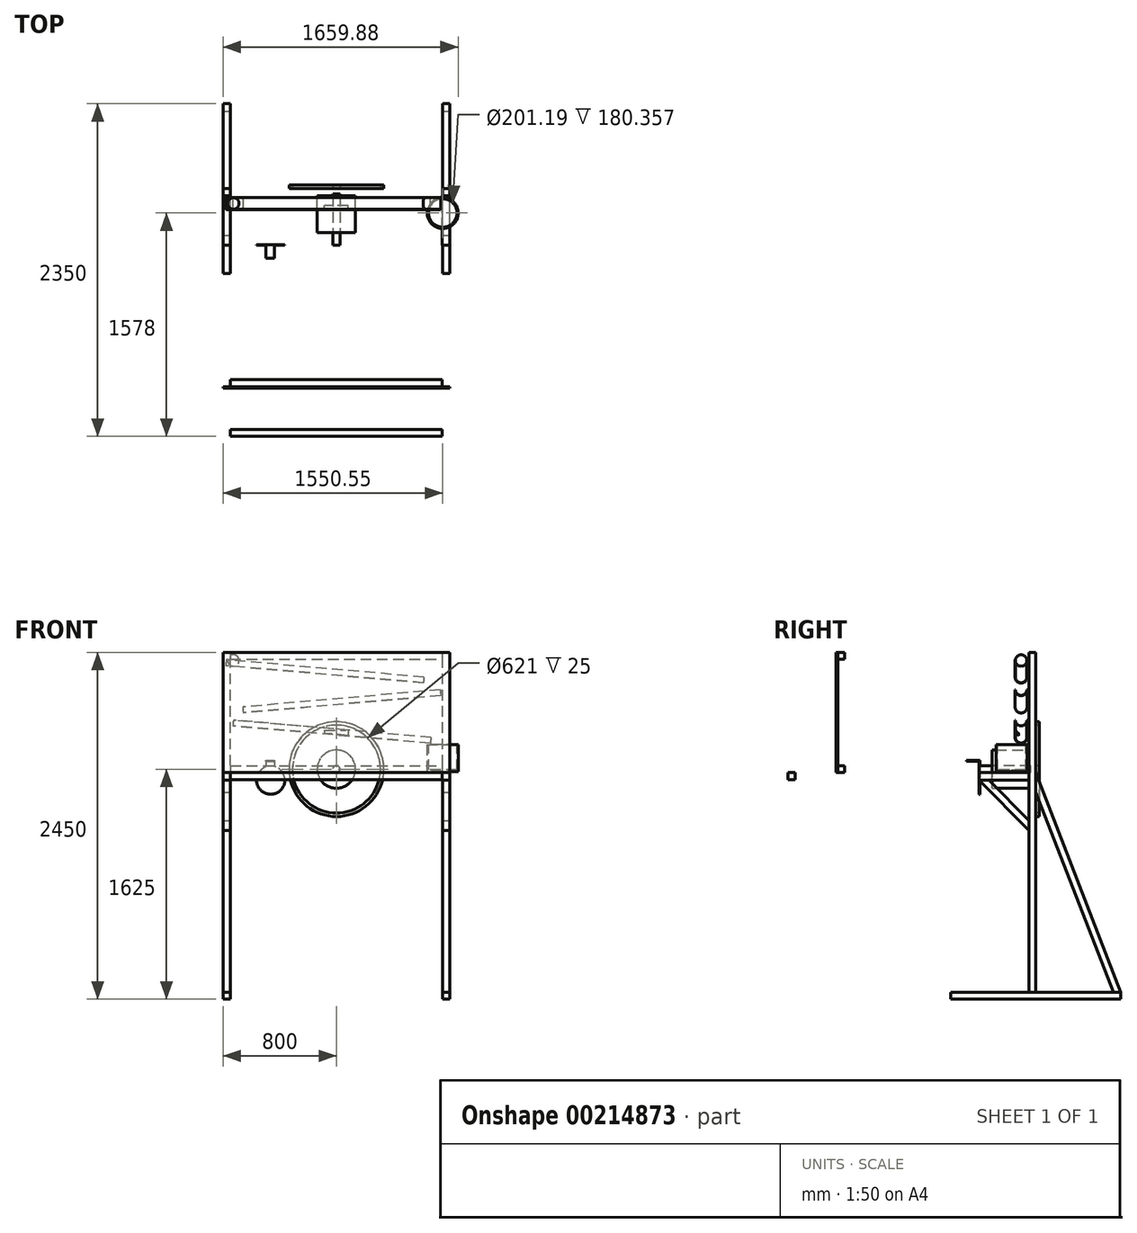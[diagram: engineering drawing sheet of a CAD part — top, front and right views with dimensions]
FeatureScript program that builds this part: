
annotation { "Feature Type Name" : "Feature", "Feature Type Description" : "" }
export const myFeature = defineFeature(function(context is Context, id is Id, definition is map)
    precondition{}
    {
        {
            var Q0;
            Q0=qCreatedBy(makeId("Front.planeOp"),FACE);
            var sketch = newSketch(context, id + "F0", { "sketchPlane" : qUnion([Q0])});
            skLineSegment(sketch, "E0.bottom", {"start": v(-225, 0) * mm, "end": v(225, 0) * mm});
            skLineSegment(sketch, "E0.top", {"start": v(-225, 450) * mm, "end": v(225, 450) * mm});
            skLineSegment(sketch, "E0.left", {"start": v(-225, 0) * mm, "end": v(-225, 450) * mm});
            skLineSegment(sketch, "E0.right", {"start": v(225, 0) * mm, "end": v(225, 450) * mm});
            skLineSegment(sketch, "E1", {"start": v(0, 450) * mm, "end": v(0, 1150) * mm});
            skEllipse(sketch, "E2", {"center": v(0, 800) * mm, "majorRadius": 350 * mm, "minorRadius": 176.3 * mm, "majorAxis": v(0, 1)});
            skLineSegment(sketch, "E3", {"start": v(0, 1150) * mm, "end": v(0, 1400) * mm});
            skCircle(sketch, "E4", {"center": v(0, 1275) * mm, "radius": 125 * mm});
            skSolve(sketch);
        }
        {
            var Q0;
            Q0=qCreatedBy(makeId("Front.planeOp"),FACE);
            var sketch = newSketch(context, id + "F1", { "sketchPlane" : qUnion([Q0])});
            skLineSegment(sketch, "E5.top", {"start": v(800, 2400) * mm, "end": v(750, 2400) * mm});
            skLineSegment(sketch, "E5.left", {"start": v(800, 0) * mm, "end": v(800, 2400) * mm});
            skLineSegment(sketch, "E5.right", {"start": v(750, 0) * mm, "end": v(750, 2400) * mm});
            skLineSegment(sketch, "E6.top", {"start": v(-800, 2400) * mm, "end": v(-750, 2400) * mm});
            skLineSegment(sketch, "E6.left", {"start": v(-800, 0) * mm, "end": v(-800, 2400) * mm});
            skLineSegment(sketch, "E6.right", {"start": v(-750, 0) * mm, "end": v(-750, 2400) * mm});
            skLineSegment(sketch, "E7.bottom", {"start": v(-749.4, 2400) * mm, "end": v(746.98, 2400) * mm});
            skLineSegment(sketch, "E7.top", {"start": v(-749.4, 2350) * mm, "end": v(746.98, 2350) * mm});
            skLineSegment(sketch, "E7.left", {"start": v(-749.4, 2400) * mm, "end": v(-749.4, 2350) * mm});
            skLineSegment(sketch, "E7.right", {"start": v(746.98, 2400) * mm, "end": v(746.98, 2350) * mm});
            skLineSegment(sketch, "E8.bottom", {"start": v(-748.32, 1600) * mm, "end": v(748.04, 1600) * mm});
            skLineSegment(sketch, "E8.top", {"start": v(-748.32, 1550) * mm, "end": v(748.04, 1550) * mm});
            skLineSegment(sketch, "E8.left", {"start": v(-748.32, 1600) * mm, "end": v(-748.32, 1550) * mm});
            skLineSegment(sketch, "E8.right", {"start": v(748.04, 1600) * mm, "end": v(748.04, 1550) * mm});
            skLineSegment(sketch, "E9", {"start": v(-800, 0) * mm, "end": v(-750, 0) * mm});
            skPoint(sketch, "E6.bottom.start.orphan", {"position": v(-800, 0) * mm});
            skLineSegment(sketch, "E10.trimOffspring", {"start": v(750, 0) * mm, "end": v(800, 0) * mm});
            skPoint(sketch, "E11.orphan", {"position": v(800, 0) * mm});
            skSolve(sketch);
        }
        {
            var Q0;
            Q0 = qSketchRegion(id + "F1", true);
            extrude(context, id + "F2", {"entities" : qUnion([Q0]), "depth" : 50 * mm, "offsetDistance" : 25 * mm});
        }
        {
            var Q0;
            Q0=makeQuery(id+"F2.opExtrude","CAP_FACE",FACE,{"disambiguationData":[OSD([sQuery(id+"F1.wireOp",EDGE,"E6.bottom"),sQuery(id+"F1.wireOp",EDGE,"E6.top"),sQuery(id+"F1.wireOp",EDGE,"E6.left"),sQuery(id+"F1.wireOp",EDGE,"E6.right")])],"isStart":false});
            var sketch = newSketch(context, id + "F3", { "sketchPlane" : qUnion([Q0])});
            skLineSegment(sketch, "E12.0", {"start": v(-748.32, 1550) * mm, "end": v(748.04, 1550) * mm, "construction": true});
            skLineSegment(sketch, "E13.0", {"start": v(800, 0) * mm, "end": v(800, 2400) * mm, "construction": true});
            skLineSegment(sketch, "E14.0", {"start": v(-800, 0) * mm, "end": v(-800, 2400) * mm, "construction": true});
            skLineSegment(sketch, "E15.bottom", {"start": v(-800, 2400) * mm, "end": v(800, 2400) * mm});
            skLineSegment(sketch, "E15.top", {"start": v(-800, 1550) * mm, "end": v(800, 1550) * mm});
            skLineSegment(sketch, "E15.left", {"start": v(-800, 2400) * mm, "end": v(-800, 1550) * mm});
            skLineSegment(sketch, "E15.right", {"start": v(800, 2400) * mm, "end": v(800, 1550) * mm});
            skSolve(sketch);
        }
        {
            var Q0;
            Q0 = qSketchRegion(id + "F3", true);
            extrude(context, id + "F4", {"entities" : qUnion([Q0]), "depth" : 10 * mm, "offsetDistance" : 25 * mm});
        }
        {
            var Q0;
            Q0=qCreatedBy(makeId("Right.planeOp"),FACE);
            var sketch = newSketch(context, id + "F5", { "sketchPlane" : qUnion([Q0])});
            skArc(sketch, "E16", {"start": v(-146.99, 2435.9) * mm, "mid": v(-104.43, 2393.34) * mm, "end": v(-61.88, 2435.9) * mm});
            skArc(sketch, "E17", {"start": v(-144.88, 2435.9) * mm, "mid": v(-104.43, 2395.46) * mm, "end": v(-64, 2435.9) * mm});
            skLineSegment(sketch, "E18", {"start": v(-64, 2435.9) * mm, "end": v(-61.88, 2435.9) * mm});
            skLineSegment(sketch, "E19", {"start": v(-144.88, 2435.9) * mm, "end": v(-146.99, 2435.9) * mm});
            skSolve(sketch);
        }
        {
            var Q0;
            Q0 = qSketchRegion(id + "F5", true);
            extrude(context, id + "F6", {"entities" : qUnion([Q0]), "endBound" : BoundingType.SYMMETRIC, "depth" : 1400 * mm, "offsetDistance" : 25 * mm});
        }
        {
            var Q0;
            Q0=makeQuery(id+"F6.opExtrude","SWEPT_BODY",BODY,{"disambiguationData":[OSD([sQuery(id+"F5.wireOp",EDGE,"E16"),sQuery(id+"F5.wireOp",EDGE,"E17"),sQuery(id+"F5.wireOp",EDGE,"E18"),sQuery(id+"F5.wireOp",EDGE,"E19")])]});
            var Q1;
            Q1=sQuery(id+"F5.wireOp",EDGE,"E19");
            transform(context, id + "F7", {"entities" : qUnion([Q0]), "transformType" : TransformType.ROTATION, "transformAxis" : qUnion([Q1]), "angle" : 5 * degree, "oppositeDirection" : true, "makeCopy" : false});
        }
        {
            var Q0;
            Q0=makeQuery(id+"F6.opExtrude","SWEPT_BODY",BODY,{"disambiguationData":[OSD([sQuery(id+"F5.wireOp",EDGE,"E16"),sQuery(id+"F5.wireOp",EDGE,"E17"),sQuery(id+"F5.wireOp",EDGE,"E18"),sQuery(id+"F5.wireOp",EDGE,"E19")])]});
            transform(context, id + "F8", {"entities" : qUnion([Q0]), "transformType" : TransformType.TRANSLATION_3D, "dx" : -80 * mm, "dy" : 0 * mm, "dz" : -150 * mm, "makeCopy" : false});
        }
        {
            var Q0;
            Q0=makeQuery(id+"F6.opExtrude","SWEPT_BODY",BODY,{"disambiguationData":[OSD([sQuery(id+"F5.wireOp",EDGE,"E16"),sQuery(id+"F5.wireOp",EDGE,"E17"),sQuery(id+"F5.wireOp",EDGE,"E18"),sQuery(id+"F5.wireOp",EDGE,"E19")])]});
            transform(context, id + "F9", {"entities" : qUnion([Q0]), "transformType" : TransformType.TRANSLATION_3D, "dx" : 116 * mm, "dy" : 0 * mm, "dz" : -89 * mm, "makeCopy" : true});
        }
        {
            var Q0;
            Q0=makeQuery(id+"F9.opPattern","COPY",BODY,{"derivedFrom":makeQuery(id+"F6.opExtrude","SWEPT_BODY",BODY,{"disambiguationData":[OSD([sQuery(id+"F5.wireOp",EDGE,"E16"),sQuery(id+"F5.wireOp",EDGE,"E17"),sQuery(id+"F5.wireOp",EDGE,"E18"),sQuery(id+"F5.wireOp",EDGE,"E19")])]}),"instanceName":"1"});
            var Q1;
            Q1=makeQuery(id+"F9.opPattern","COPY",EDGE,{"derivedFrom":makeQuery(id+"F6.opExtrude","CAP_EDGE",EDGE,{"disambiguationData":[OSD([sQuery(id+"F5.wireOp",EDGE,"E19")])],"isStart":false}),"instanceName":"1"});
            transform(context, id + "F10", {"entities" : qUnion([Q0]), "transformType" : TransformType.ROTATION, "transformAxis" : qUnion([Q1]), "angle" : 10 * degree, "makeCopy" : false});
        }
        {
            var Q0;
            Q0=makeQuery(id+"F6.opExtrude","SWEPT_BODY",BODY,{"disambiguationData":[OSD([sQuery(id+"F5.wireOp",EDGE,"E16"),sQuery(id+"F5.wireOp",EDGE,"E17"),sQuery(id+"F5.wireOp",EDGE,"E18"),sQuery(id+"F5.wireOp",EDGE,"E19")])]});
            transform(context, id + "F11", {"entities" : qUnion([Q0]), "transformType" : TransformType.TRANSLATION_3D, "dx" : 50 * mm, "dy" : 0 * mm, "dz" : -426 * mm, "makeCopy" : true});
        }
        {
            var Q0;
            Q0=makeQuery(id+"F2.opExtrude","CAP_FACE",FACE,{"disambiguationData":[OSD([sQuery(id+"F1.wireOp",EDGE,"E5.bottom"),sQuery(id+"F1.wireOp",EDGE,"E5.top"),sQuery(id+"F1.wireOp",EDGE,"E5.left"),sQuery(id+"F1.wireOp",EDGE,"E5.right")])],"isStart":false});
            var sketch = newSketch(context, id + "F12", { "sketchPlane" : qUnion([Q0])});
            skCircle(sketch, "E20", {"center": v(0, 1575) * mm, "radius": 135 * mm});
            skSolve(sketch);
        }
        {
            var Q0;
            Q0 = qSketchRegion(id + "F12", true);
            extrude(context, id + "F13", {"entities" : qUnion([Q0]), "depth" : 260 * mm, "offsetDistance" : 25 * mm});
        }
        {
            var Q0;
            Q0=makeQuery(id+"F2.opExtrude","CAP_FACE",FACE,{"disambiguationData":[OSD([sQuery(id+"F1.wireOp",EDGE,"E5.bottom"),sQuery(id+"F1.wireOp",EDGE,"E5.top"),sQuery(id+"F1.wireOp",EDGE,"E5.left"),sQuery(id+"F1.wireOp",EDGE,"E5.right")])],"isStart":false});
            cPlane(context, id + "F14", {"entities" : qUnion([Q0]), "cplaneType" : CPlaneType.OFFSET, "offset" : 130 * mm, "width" : 150 * mm, "height" : 150 * mm});
        }
        {
            var Q0;
            Q0=qCreatedBy(id+"F14.planeOp",FACE);
            var sketch = newSketch(context, id + "F15", { "sketchPlane" : qUnion([Q0])});
            skLineSegment(sketch, "E21.bottom", {"start": v(-84.82, 1851.31) * mm, "end": v(82.61, 1851.31) * mm});
            skLineSegment(sketch, "E21.top", {"start": v(-84.82, 1762.65) * mm, "end": v(82.61, 1762.65) * mm});
            skLineSegment(sketch, "E21.left", {"start": v(-84.82, 1851.31) * mm, "end": v(-84.82, 1762.65) * mm});
            skLineSegment(sketch, "E21.right", {"start": v(82.61, 1851.31) * mm, "end": v(82.61, 1762.65) * mm});
            skSolve(sketch);
        }
        {
            var Q0;
            Q0 = qSketchRegion(id + "F15", true);
            extrude(context, id + "F16", {"entities" : qUnion([Q0]), "operationType" : NewBodyOperationType.REMOVE, "endBound" : BoundingType.SYMMETRIC, "depth" : 118 * mm, "offsetDistance" : 25 * mm});
        }
        {
            var Q0;
            Q0=makeQuery(id+"F2.opExtrude","SWEPT_BODY",BODY,{"disambiguationData":[OSD([sQuery(id+"F1.wireOp",EDGE,"E8.bottom"),sQuery(id+"F1.wireOp",EDGE,"E8.top"),sQuery(id+"F1.wireOp",EDGE,"E8.left"),sQuery(id+"F1.wireOp",EDGE,"E8.right")])]});
            transform(context, id + "F17", {"entities" : qUnion([Q0]), "transformType" : TransformType.TRANSLATION_3D, "dx" : 0 * mm, "dy" : -350 * mm, "dz" : -50 * mm, "makeCopy" : true});
        }
        {
            var Q0;
            Q0=makeQuery(id+"F2.opExtrude","CAP_FACE",FACE,{"disambiguationData":[OSD([sQuery(id+"F1.wireOp",EDGE,"E5.bottom"),sQuery(id+"F1.wireOp",EDGE,"E5.top"),sQuery(id+"F1.wireOp",EDGE,"E5.left"),sQuery(id+"F1.wireOp",EDGE,"E5.right")])],"isStart":false});
            var sketch = newSketch(context, id + "F18", { "sketchPlane" : qUnion([Q0])});
            skLineSegment(sketch, "E22.0", {"start": v(-800, 2400) * mm, "end": v(-800, 2400) * mm});
            skLineSegment(sketch, "E23.0", {"start": v(-748.32, 1550) * mm, "end": v(748.04, 1550) * mm, "construction": true});
            skLineSegment(sketch, "E24.0", {"start": v(-748.32, 1600) * mm, "end": v(748.04, 1600) * mm, "construction": true});
            skLineSegment(sketch, "E25.0", {"start": v(-750, 2400) * mm, "end": v(-750, 2400) * mm});
            skLineSegment(sketch, "E26.0", {"start": v(750, 2400) * mm, "end": v(750, 2400) * mm});
            skLineSegment(sketch, "E27.0", {"start": v(800, 2400) * mm, "end": v(800, 2400) * mm});
            skLineSegment(sketch, "E28.0", {"start": v(-800, 0) * mm, "end": v(-800, 2400) * mm, "construction": true});
            skLineSegment(sketch, "E29.0", {"start": v(800, 0) * mm, "end": v(800, 2400) * mm, "construction": true});
            skLineSegment(sketch, "E30.bottom", {"start": v(-748.32, 1550) * mm, "end": v(-800, 1550) * mm});
            skLineSegment(sketch, "E30.top", {"start": v(-748.32, 1498.04) * mm, "end": v(-800, 1498.04) * mm});
            skLineSegment(sketch, "E30.left", {"start": v(-748.32, 1550) * mm, "end": v(-748.32, 1498.04) * mm});
            skLineSegment(sketch, "E30.right", {"start": v(-800, 1550) * mm, "end": v(-800, 1498.04) * mm});
            skPoint(sketch, "E31.oppositeSnap0", {"position": v(-774.16, 1498.04) * mm});
            skLineSegment(sketch, "E31.bottom", {"start": v(748.04, 1550) * mm, "end": v(800, 1550) * mm});
            skLineSegment(sketch, "E31.top", {"start": v(748.04, 1498.04) * mm, "end": v(800, 1498.04) * mm});
            skLineSegment(sketch, "E31.left", {"start": v(748.04, 1550) * mm, "end": v(748.04, 1498.04) * mm});
            skLineSegment(sketch, "E31.right", {"start": v(800, 1550) * mm, "end": v(800, 1498.04) * mm});
            skSolve(sketch);
        }
        {
            var Q0;
            Q0 = qSketchRegion(id + "F18", true);
            extrude(context, id + "F19", {"entities" : qUnion([Q0]), "depth" : 350 * mm, "offsetDistance" : 25 * mm});
        }
        {
            var Q0;
            Q0=makeQuery(id+"F2.opExtrude","SWEPT_FACE",FACE,{"disambiguationData":[OSD([sQuery(id+"F1.wireOp",EDGE,"E5.left")])]});
            var sketch = newSketch(context, id + "F20", { "sketchPlane" : qUnion([Q0])});
            skPoint(sketch, "E32.orphan", {"position": v(-60, 2500) * mm});
            skLineSegment(sketch, "E33.0", {"start": v(-400, 1498.04) * mm, "end": v(-329.99, 1498.04) * mm});
            skLineSegment(sketch, "E34.0", {"start": v(-50, 1140.96) * mm, "end": v(-50, 1212.4) * mm});
            skLineSegment(sketch, "E35", {"start": v(-400, 1498.04) * mm, "end": v(-50, 1140.96) * mm});
            skLineSegment(sketch, "E36.0", {"start": v(-329.99, 1498.04) * mm, "end": v(-50, 1212.4) * mm});
            skPoint(sketch, "E37.orphan", {"position": v(-50, 0) * mm});
            skSolve(sketch);
        }
        {
            var Q0;
            Q0 = qSketchRegion(id + "F20", true);
            extrude(context, id + "F21", {"entities" : qUnion([Q0]), "oppositeDirection" : true, "depth" : 50 * mm, "offsetDistance" : 25 * mm});
        }
        {
            var Q0;
            Q0=makeQuery(id+"F21.opExtrude","SWEPT_BODY",BODY,{"disambiguationData":[OSD([sQuery(id+"F20.wireOp",EDGE,"E33.0"),sQuery(id+"F20.wireOp",EDGE,"E34.0"),sQuery(id+"F20.wireOp",EDGE,"E35"),sQuery(id+"F20.wireOp",EDGE,"E36.0")])]});
            transform(context, id + "F22", {"entities" : qUnion([Q0]), "transformType" : TransformType.TRANSLATION_3D, "dx" : -1550 * mm, "dy" : 0 * mm, "dz" : 0 * mm, "makeCopy" : true});
        }
        {
            var Q0;
            Q0=makeQuery(id+"F17.opPattern","COPY",FACE,{"derivedFrom":makeQuery(id+"F2.opExtrude","CAP_FACE",FACE,{"disambiguationData":[OSD([sQuery(id+"F1.wireOp",EDGE,"E8.bottom"),sQuery(id+"F1.wireOp",EDGE,"E8.top"),sQuery(id+"F1.wireOp",EDGE,"E8.left"),sQuery(id+"F1.wireOp",EDGE,"E8.right")])],"isStart":false}),"instanceName":"1"});
            var sketch = newSketch(context, id + "F23", { "sketchPlane" : qUnion([Q0])});
            skCircle(sketch, "E38.0", {"center": v(0, 1575) * mm, "radius": 135 * mm, "construction": true});
            skCircle(sketch, "E39", {"center": v(0, 1575) * mm, "radius": 25 * mm});
            skSolve(sketch);
        }
        {
            var Q0;
            Q0 = qSketchRegion(id + "F23", true);
            extrude(context, id + "F24", {"entities" : qUnion([Q0]), "oppositeDirection" : true, "depth" : 363 * mm, "offsetDistance" : 25 * mm});
        }
        {
            var Q0;
            Q0=qCreatedBy(makeId("Front.planeOp"),FACE);
            var sketch = newSketch(context, id + "F25", { "sketchPlane" : qUnion([Q0])});
            skLineSegment(sketch, "E40.0", {"start": v(-800, 0) * mm, "end": v(-750, 0) * mm});
            skLineSegment(sketch, "E41.0", {"start": v(750, 0) * mm, "end": v(800, 0) * mm});
            skLineSegment(sketch, "E42", {"start": v(800, 0) * mm, "end": v(800, -50) * mm});
            skLineSegment(sketch, "E43", {"start": v(800, -50) * mm, "end": v(750, -50) * mm});
            skLineSegment(sketch, "E44", {"start": v(750, -50) * mm, "end": v(750, 0) * mm});
            skLineSegment(sketch, "E45", {"start": v(-800, 0) * mm, "end": v(-800, -50) * mm});
            skPoint(sketch, "E45.endSnap0", {"position": v(775, -50) * mm});
            skLineSegment(sketch, "E46", {"start": v(-800, -50) * mm, "end": v(-750, -50) * mm});
            skLineSegment(sketch, "E47", {"start": v(-750, -50) * mm, "end": v(-750, 0) * mm});
            skSolve(sketch);
        }
        {
            var Q0;
            Q0 = qSketchRegion(id + "F25", true);
            extrude(context, id + "F26", {"entities" : qUnion([Q0]), "endBound" : BoundingType.SYMMETRIC, "depth" : 1200 * mm, "offsetDistance" : 25 * mm});
        }
        {
            var Q0;
            Q0=makeQuery(id+"F2.opExtrude","SWEPT_FACE",FACE,{"disambiguationData":[OSD([sQuery(id+"F1.wireOp",EDGE,"E5.left")])]});
            var sketch = newSketch(context, id + "F27", { "sketchPlane" : qUnion([Q0])});
            skLineSegment(sketch, "E48.0", {"start": v(0, 1411.5) * mm, "end": v(0, 1550) * mm});
            skLineSegment(sketch, "E49", {"start": v(0, 1550) * mm, "end": v(600, 0) * mm});
            skLineSegment(sketch, "E50.0", {"start": v(0, 1411.5) * mm, "end": v(546.38, 0) * mm});
            skLineSegment(sketch, "E51.trimOffspring", {"start": v(546.38, 0) * mm, "end": v(600, 0) * mm});
            skLineSegment(sketch, "E52.0", {"start": v(-600, 0) * mm, "end": v(600, 0) * mm, "construction": true});
            skLineSegment(sketch, "E53.0", {"start": v(-400, 1550) * mm, "end": v(-50, 1550) * mm, "construction": true});
            skSolve(sketch);
        }
        {
            var Q0;
            Q0 = qSketchRegion(id + "F27", true);
            extrude(context, id + "F28", {"entities" : qUnion([Q0]), "oppositeDirection" : true, "depth" : 50 * mm, "offsetDistance" : 25 * mm});
        }
        {
            var Q0;
            Q0=makeQuery(id+"F28.opExtrude","SWEPT_BODY",BODY,{"disambiguationData":[OSD([sQuery(id+"F27.wireOp",EDGE,"E48.0"),sQuery(id+"F27.wireOp",EDGE,"E49"),sQuery(id+"F27.wireOp",EDGE,"E50.0"),sQuery(id+"F27.wireOp",EDGE,"E51.trimOffspring")])]});
            transform(context, id + "F29", {"entities" : qUnion([Q0]), "transformType" : TransformType.TRANSLATION_3D, "dx" : -1550 * mm, "dy" : 0 * mm, "dz" : 0 * mm, "makeCopy" : true});
        }
        {
            var Q0;
            Q0=makeQuery(id+"F17.opPattern","COPY",FACE,{"derivedFrom":makeQuery(id+"F2.opExtrude","CAP_FACE",FACE,{"disambiguationData":[OSD([sQuery(id+"F1.wireOp",EDGE,"E8.bottom"),sQuery(id+"F1.wireOp",EDGE,"E8.top"),sQuery(id+"F1.wireOp",EDGE,"E8.left"),sQuery(id+"F1.wireOp",EDGE,"E8.right")])],"isStart":false}),"instanceName":"1"});
            var sketch = newSketch(context, id + "F30", { "sketchPlane" : qUnion([Q0])});
            skArc(sketch, "E54", {"start": v(-496.72, 1591.77) * mm, "mid": v(-460.45, 1397.34) * mm, "end": v(-437.98, 1593.84) * mm});
            skLineSegment(sketch, "E55.bottom", {"start": v(-496.72, 1632.1) * mm, "end": v(-437.98, 1632.1) * mm});
            skLineSegment(sketch, "E55.left", {"start": v(-496.72, 1632.1) * mm, "end": v(-496.72, 1591.77) * mm});
            skLineSegment(sketch, "E55.right", {"start": v(-437.98, 1632.1) * mm, "end": v(-437.98, 1593.84) * mm});
            skSolve(sketch);
        }
        {
            var Q0;
            Q0 = qSketchRegion(id + "F30", true);
            extrude(context, id + "F31", {"entities" : qUnion([Q0]), "oppositeDirection" : true, "depth" : 5 * mm, "offsetDistance" : 25 * mm});
        }
        {
            var Q0;
            Q0=makeQuery(id+"F31.opExtrude","SWEPT_FACE",FACE,{"disambiguationData":[OSD([sQuery(id+"F30.wireOp",EDGE,"E55.right")])]});
            var sketch = newSketch(context, id + "F32", { "sketchPlane" : qUnion([Q0])});
            skLineSegment(sketch, "E56.0", {"start": v(-395, 1632.1) * mm, "end": v(-400, 1632.1) * mm});
            skLineSegment(sketch, "E57.bottom", {"start": v(-395, 1632.1) * mm, "end": v(-490.69, 1632.1) * mm});
            skLineSegment(sketch, "E57.top", {"start": v(-395, 1636.8) * mm, "end": v(-490.69, 1636.8) * mm});
            skLineSegment(sketch, "E57.left", {"start": v(-395, 1632.1) * mm, "end": v(-395, 1636.8) * mm});
            skLineSegment(sketch, "E57.right", {"start": v(-490.69, 1632.1) * mm, "end": v(-490.69, 1636.8) * mm});
            skSolve(sketch);
        }
        {
            var Q0;
            Q0 = qSketchRegion(id + "F32", true);
            var Q1;
            Q1 = qConstructionFilter(qBodyType(qCreatedBy(id + "F32" ,EDGE), BodyType.WIRE), ConstructionObject.NO);
            var Q2;
            Q2=makeQuery(id+"F31.opExtrude","SWEPT_FACE",FACE,{"disambiguationData":[OSD([sQuery(id+"F30.wireOp",EDGE,"E55.left")])]});
            extrude(context, id + "F33", {"entities" : qUnion([Q0]), "operationType" : NewBodyOperationType.ADD, "surfaceOperationType" : NewSurfaceOperationType.ADD, "surfaceEntities" : qUnion([Q1]), "endBound" : BoundingType.UP_TO_SURFACE, "oppositeDirection" : true, "depth" : 25 * mm, "endBoundEntityFace" : qUnion([Q2]), "offsetDistance" : 25 * mm});
        }
        {
            var Q0;
            Q0=makeQuery(id+"F6.opExtrude","CAP_FACE",FACE,{"disambiguationData":[OSD([sQuery(id+"F5.wireOp",EDGE,"E16"),sQuery(id+"F5.wireOp",EDGE,"E17"),sQuery(id+"F5.wireOp",EDGE,"E18"),sQuery(id+"F5.wireOp",EDGE,"E19")])],"isStart":true});
            cPlane(context, id + "F34", {"entities" : qUnion([Q0]), "cplaneType" : CPlaneType.OFFSET, "offset" : 50 * mm, "oppositeDirection" : true, "width" : 150 * mm, "height" : 150 * mm});
        }
        {
            var Q0;
            Q0=qCreatedBy(id+"F34.planeOp",FACE);
            var sketch = newSketch(context, id + "F35", { "sketchPlane" : qUnion([Q0])});
            skArc(sketch, "E58.0", {"start": v(144.88, 2270.23) * mm, "mid": v(104.43, 2229.79) * mm, "end": v(64, 2270.23) * mm});
            skLineSegment(sketch, "E59", {"start": v(64, 2270.23) * mm, "end": v(144.88, 2270.23) * mm});
            skSolve(sketch);
        }
        {
            var Q0;
            Q0 = qSketchRegion(id + "F35", true);
            var Q1;
            Q1=sQuery(id+"F35.wireOp",EDGE,"E59");
            revolve(context, id + "F36", {"surfaceOperationType" : NewSurfaceOperationType.NEW, "entities" : qUnion([Q0]), "axis" : qUnion([Q1]), "revolveType" : RevolveType.FULL});
        }
        {
            var Q0;
            Q0=makeQuery(id+"F2.opExtrude","CAP_FACE",FACE,{"disambiguationData":[OSD([sQuery(id+"F1.wireOp",EDGE,"E8.bottom"),sQuery(id+"F1.wireOp",EDGE,"E8.top"),sQuery(id+"F1.wireOp",EDGE,"E8.left"),sQuery(id+"F1.wireOp",EDGE,"E8.right")])],"isStart":true});
            var sketch = newSketch(context, id + "F37", { "sketchPlane" : qUnion([Q0])});
            skCircle(sketch, "E60.0", {"center": v(0, 1575) * mm, "radius": 25 * mm});
            skCircle(sketch, "E61", {"center": v(0, 1575) * mm, "radius": 334.6 * mm});
            skCircle(sketch, "E62", {"center": v(0, 1575) * mm, "radius": 310.5 * mm});
            skSolve(sketch);
        }
        {
            var Q0;
            Q0 = qSketchRegion(id + "F37", true);
            var Q1;
            Q1=makeQuery(id+"F37.imprint","IMPRINT",FACE,{"disambiguationData":[TD([[makeQuery(id+"F37.imprint","IMPRINT",EDGE,{"derivedFrom":sQuery(id+"F37.wireOp",EDGE,"E60.0")}),1.0]])]});
            extrude(context, id + "F38", {"entities" : qUnion([Q0, Q1]), "depth" : 25 * mm, "offsetDistance" : 25 * mm});
        }
        {
            var Q0;
            Q0=makeQuery(id+"F38.opExtrude","CAP_FACE",FACE,{"disambiguationData":[OSD([sQuery(id+"F37.wireOp",EDGE,"E61"),sQuery(id+"F37.wireOp",EDGE,"E62")])],"isStart":false});
            cPlane(context, id + "F39", {"entities" : qUnion([Q0]), "cplaneType" : CPlaneType.OFFSET, "offset" : 12.5 * mm, "oppositeDirection" : true, "width" : 150 * mm, "height" : 150 * mm});
        }
        {
            var Q0;
            Q0=qCreatedBy(makeId("Front.planeOp"),FACE);
            var sketch = newSketch(context, id + "F40", { "sketchPlane" : qUnion([Q0])});
            skLineSegment(sketch, "E63.bottom", {"start": v(694.14, 1547.35) * mm, "end": v(702.88, 1547.35) * mm});
            skLineSegment(sketch, "E63.top", {"start": v(593.55, 1355.9) * mm, "end": v(702.88, 1355.9) * mm});
            skLineSegment(sketch, "E63.left", {"start": v(593.55, 1367) * mm, "end": v(593.55, 1355.9) * mm});
            skLineSegment(sketch, "E63.right", {"start": v(702.88, 1547.35) * mm, "end": v(702.88, 1355.9) * mm});
            skLineSegment(sketch, "E64.bottom", {"start": v(593.55, 1367) * mm, "end": v(694.14, 1367) * mm});
            skLineSegment(sketch, "E64.right", {"start": v(694.14, 1367) * mm, "end": v(694.14, 1547.35) * mm});
            skSolve(sketch);
        }
        {
            var Q0;
            Q0 = qSketchRegion(id + "F40", true);
            var Q1;
            Q1=sQuery(id+"F40.wireOp",EDGE,"E63.left");
            revolve(context, id + "F41", {"surfaceOperationType" : NewSurfaceOperationType.NEW, "entities" : qUnion([Q0]), "axis" : qUnion([Q1]), "revolveType" : RevolveType.FULL});
        }
        {
            var Q0;
            Q0=makeQuery(id+"F41.opRevolve","SWEPT_BODY",BODY,{"disambiguationData":[OSD([sQuery(id+"F40.wireOp",EDGE,"E63.bottom"),sQuery(id+"F40.wireOp",EDGE,"E63.top"),sQuery(id+"F40.wireOp",EDGE,"E63.left"),sQuery(id+"F40.wireOp",EDGE,"E63.right"),sQuery(id+"F40.wireOp",EDGE,"E64.bottom"),sQuery(id+"F40.wireOp",EDGE,"E64.right")])]});
            transform(context, id + "F42", {"entities" : qUnion([Q0]), "transformType" : TransformType.TRANSLATION_3D, "dx" : 157 * mm, "dy" : -172 * mm, "dz" : 202 * mm, "makeCopy" : false});
        }
        {
            var Q0;
            Q0=makeQuery(id+"F17.opPattern","COPY",BODY,{"derivedFrom":makeQuery(id+"F2.opExtrude","SWEPT_BODY",BODY,{"disambiguationData":[OSD([sQuery(id+"F1.wireOp",EDGE,"E8.bottom"),sQuery(id+"F1.wireOp",EDGE,"E8.top"),sQuery(id+"F1.wireOp",EDGE,"E8.left"),sQuery(id+"F1.wireOp",EDGE,"E8.right")])]}),"instanceName":"1"});
            var Q1;
            Q1=makeQuery(id+"F4.opExtrude","SWEPT_BODY",BODY,{"disambiguationData":[OSD([sQuery(id+"F3.wireOp",EDGE,"E15.bottom"),sQuery(id+"F3.wireOp",EDGE,"E15.top"),sQuery(id+"F3.wireOp",EDGE,"E15.left"),sQuery(id+"F3.wireOp",EDGE,"E15.right")])]});
            var Q2;
            Q2=makeQuery(id+"F2.opExtrude","SWEPT_BODY",BODY,{"disambiguationData":[OSD([sQuery(id+"F1.wireOp",EDGE,"E7.bottom"),sQuery(id+"F1.wireOp",EDGE,"E7.top"),sQuery(id+"F1.wireOp",EDGE,"E7.left"),sQuery(id+"F1.wireOp",EDGE,"E7.right")])]});
            var Q3;
            Q3=makeQuery(id+"F2.opExtrude","SWEPT_BODY",BODY,{"disambiguationData":[OSD([sQuery(id+"F1.wireOp",EDGE,"E8.bottom"),sQuery(id+"F1.wireOp",EDGE,"E8.top"),sQuery(id+"F1.wireOp",EDGE,"E8.left"),sQuery(id+"F1.wireOp",EDGE,"E8.right")])]});
            transform(context, id + "F43", {"entities" : qUnion([Q0, Q1, Q2, Q3]), "transformType" : TransformType.TRANSLATION_3D, "dx" : 0 * mm, "dy" : -1350 * mm, "dz" : 0 * mm, "makeCopy" : false});
        }
    });
